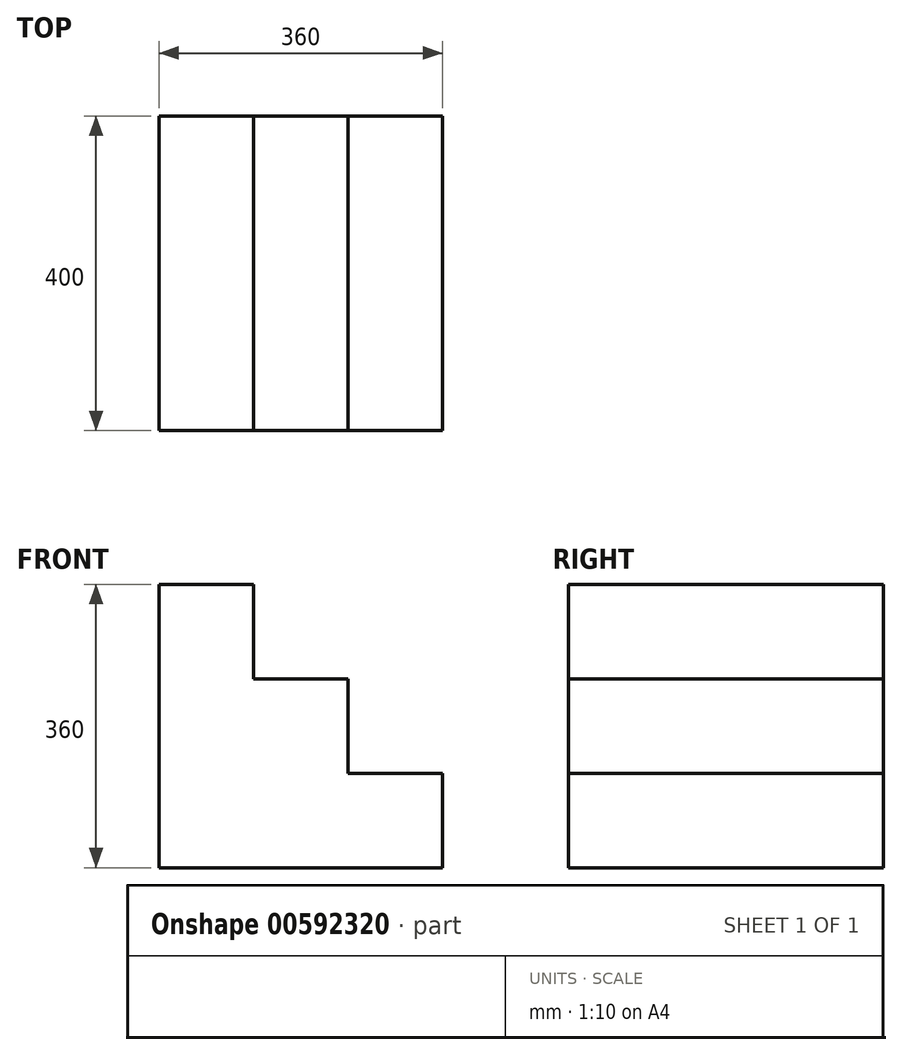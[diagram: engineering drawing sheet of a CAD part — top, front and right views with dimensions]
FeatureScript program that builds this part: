
annotation { "Feature Type Name" : "Feature", "Feature Type Description" : "" }
export const myFeature = defineFeature(function(context is Context, id is Id, definition is map)
    precondition{}
    {
        {
            var Q0;
            Q0=qCreatedBy(makeId("Front.planeOp"),FACE);
            var sketch = newSketch(context, id + "F0", { "sketchPlane" : qUnion([Q0])});
            skLineSegment(sketch, "E0", {"start": v(0, 0) * mm, "end": v(0, 360) * mm});
            skLineSegment(sketch, "E1", {"start": v(0, 0) * mm, "end": v(360, 0) * mm});
            skLineSegment(sketch, "E2", {"start": v(0, 360) * mm, "end": v(120, 360) * mm});
            skLineSegment(sketch, "E3", {"start": v(120, 360) * mm, "end": v(120, 240) * mm});
            skLineSegment(sketch, "E4", {"start": v(120, 240) * mm, "end": v(240, 240) * mm});
            skLineSegment(sketch, "E5", {"start": v(240, 240) * mm, "end": v(240, 120) * mm});
            skLineSegment(sketch, "E6", {"start": v(240, 120) * mm, "end": v(360, 120) * mm});
            skLineSegment(sketch, "E7", {"start": v(360, 120) * mm, "end": v(360, 0) * mm});
            skSolve(sketch);
        }
        {
            var Q0;
            Q0=makeQuery(id+"F0.imprint","IMPRINT",FACE,{"disambiguationData":[TD([[makeQuery(id+"F0.imprint","IMPRINT",EDGE,{"derivedFrom":sQuery(id+"F0.wireOp",EDGE,"E0")}),-1.0]])]});
            extrude(context, id + "F1", {"entities" : qUnion([Q0]), "depth" : 400 * mm, "offsetDistance" : 25 * mm});
        }
    });
